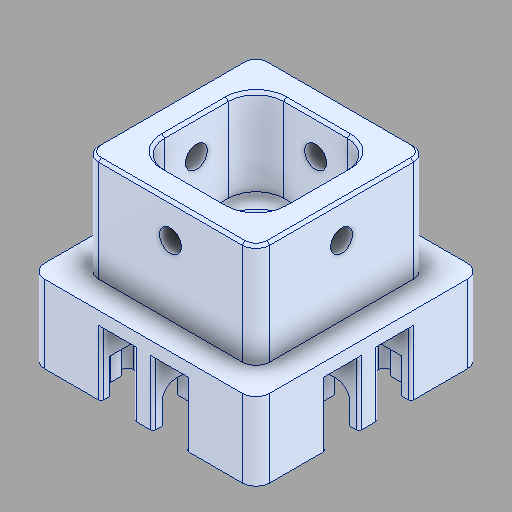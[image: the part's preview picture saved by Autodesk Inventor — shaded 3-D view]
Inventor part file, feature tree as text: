
AUTODESK INVENTOR PART (.ipt)
format: ipt  version: 2024.2 (Build 282272000, 272)  size: 302,080 bytes
history: native  units: in
note: dims shown in document units (in); Inventor stores cm internally (conversion verified against a paired STEP export)
features: fillet x1
ambient origin geometry x8: Origin, YZ Plane, XZ Plane, XY Plane, X Axis, Y Axis, Z Axis, Center Point
bodies: Solid1 (feature_tree)
feature tree (1):
  fillet  "Fillet6"  [1 undecoded]
note: 1 required parameter value undecoded (feature->parameter linkage not recoverable at this tier; creation-order binding heuristic only, values carry confidence <= 0.55)
